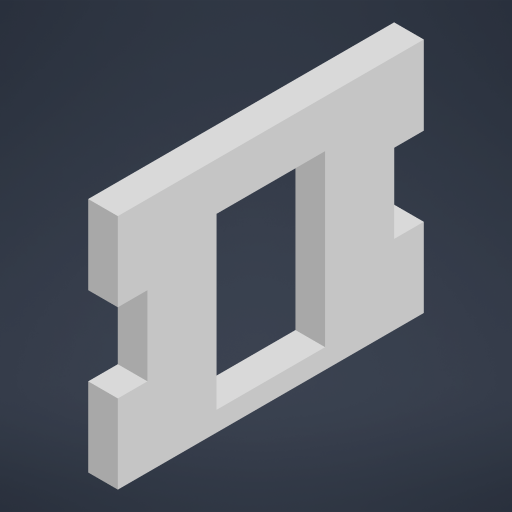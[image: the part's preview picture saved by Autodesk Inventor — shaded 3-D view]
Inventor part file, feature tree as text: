
AUTODESK INVENTOR PART (.ipt)
format: ipt  version: 2023 (Build 270158000, 158)  size: 180,224 bytes
history: native  units: mm
features: extrude x1, sketch x1
ambient origin geometry x8: Origin, YZ Plane, XZ Plane, XY Plane, X Axis, Y Axis, Z Axis, Center Point
bodies: Solid1 (feature_tree)
feature tree (2):
  extrude  "Extrusion1"  Depth=25.0mm
  sketch  "Sketch1"  dims[d0=24.0mm d1=25.0mm d2=3.0mm d3=0.0mm d4=4.8mm d5=7.0mm d6=7.0mm d7=2.0mm d8=3.0mm d9=8.0mm d10=3.0mm d11=8.0mm]
